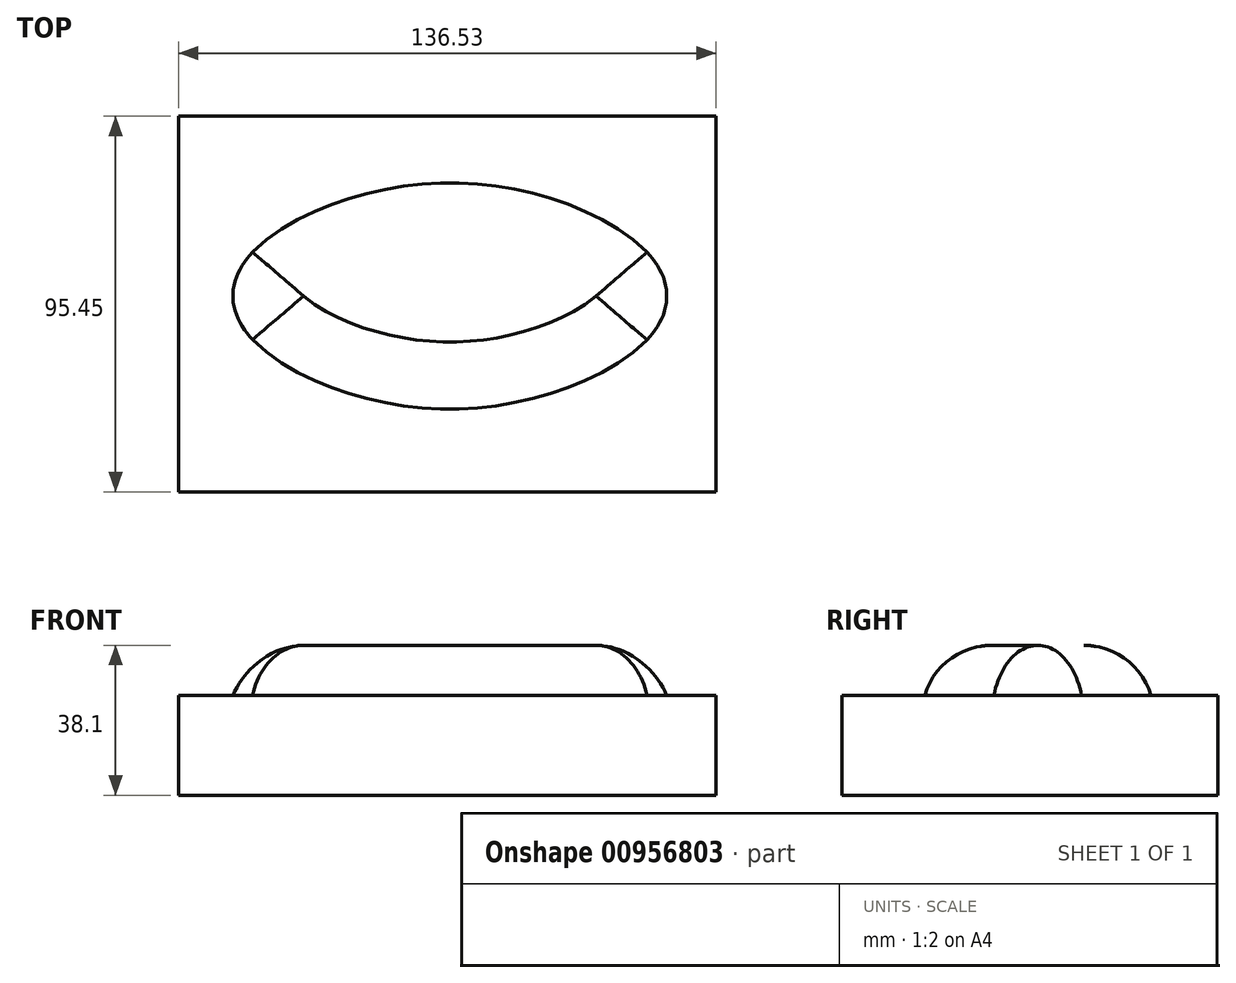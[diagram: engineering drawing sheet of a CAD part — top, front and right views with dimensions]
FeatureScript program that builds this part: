
annotation { "Feature Type Name" : "Feature", "Feature Type Description" : "" }
export const myFeature = defineFeature(function(context is Context, id is Id, definition is map)
    precondition{}
    {
        {
            var Q0;
            Q0=qCreatedBy(makeId("Top.planeOp"),FACE);
            var sketch = newSketch(context, id + "F0", { "sketchPlane" : qUnion([Q0])});
            skFitSpline(sketch, "E0", {"points": [v(-56.23, 0) * mm, v(0, 29.47) * mm, v(56.24, 0) * mm, v(0, -29.47) * mm, v(-56.23, 0) * mm]});
            skSolve(sketch);
        }
        {
            var Q0;
            Q0 = qSketchRegion(id + "F0", true);
            extrude(context, id + "F1", {"entities" : qUnion([Q0]), "depth" : 38.1 * mm, "offsetDistance" : 25.4 * mm});
        }
        {
            var Q0;
            Q0=makeQuery(id+"F1.opExtrude","SWEPT_FACE",FACE,{"disambiguationData":[OSD([sQuery(id+"F0.wireOp",EDGE,"E0")])]});
            fillet(context, id + "F2", {"entities" : qUnion([Q0]), "radius" : 17.78 * mm, "tangentPropagation" : true, "allowEdgeOverflow" : false});
        }
        {
            var Q0;
            Q0=qCreatedBy(makeId("Top.planeOp"),FACE);
            var sketch = newSketch(context, id + "F3", { "sketchPlane" : qUnion([Q0])});
            skLineSegment(sketch, "E1.bottom", {"start": v(-68.91, -49.76) * mm, "end": v(67.62, -49.76) * mm});
            skLineSegment(sketch, "E1.top", {"start": v(-68.91, 45.7) * mm, "end": v(67.62, 45.7) * mm});
            skLineSegment(sketch, "E1.left", {"start": v(-68.91, -49.76) * mm, "end": v(-68.91, 45.7) * mm});
            skLineSegment(sketch, "E1.right", {"start": v(67.62, -49.76) * mm, "end": v(67.62, 45.7) * mm});
            skSolve(sketch);
        }
        {
            var Q0;
            Q0 = qSketchRegion(id + "F3", true);
            extrude(context, id + "F4", {"entities" : qUnion([Q0]), "operationType" : NewBodyOperationType.ADD, "depth" : 25.4 * mm, "offsetDistance" : 25.4 * mm});
        }
    });
